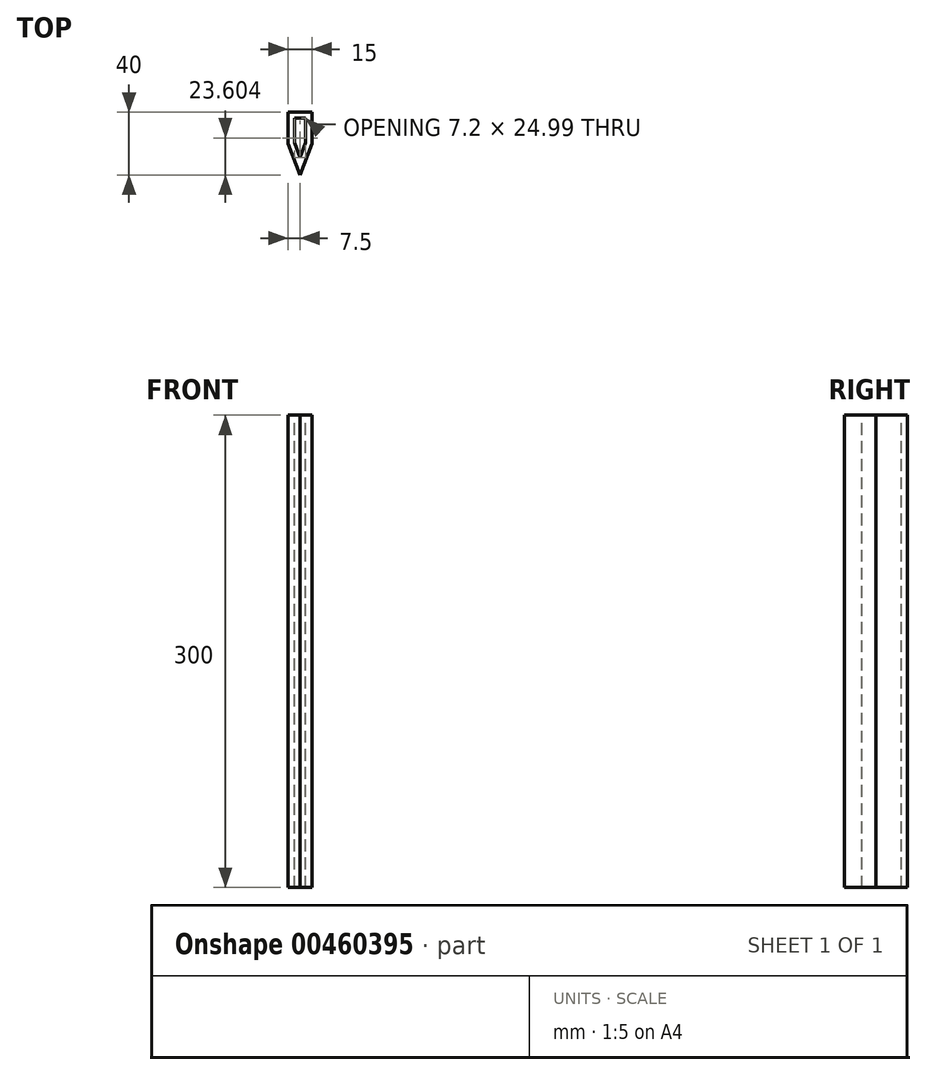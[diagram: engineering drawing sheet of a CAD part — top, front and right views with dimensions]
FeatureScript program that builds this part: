
annotation { "Feature Type Name" : "Feature", "Feature Type Description" : "" }
export const myFeature = defineFeature(function(context is Context, id is Id, definition is map)
    precondition{}
    {
        {
            var Q0;
            Q0=qCreatedBy(makeId("Top.planeOp"),FACE);
            var sketch = newSketch(context, id + "F0", { "sketchPlane" : qUnion([Q0])});
            skLineSegment(sketch, "E0", {"start": v(-7.5, 0) * mm, "end": v(-7.5, 20) * mm});
            skLineSegment(sketch, "E1", {"start": v(-7.5, 20) * mm, "end": v(7.5, 20) * mm});
            skLineSegment(sketch, "E2", {"start": v(7.5, 20) * mm, "end": v(7.5, 0) * mm});
            skLineSegment(sketch, "E3", {"start": v(7.5, 0) * mm, "end": v(0, -20) * mm});
            skLineSegment(sketch, "E4", {"start": v(0, -20) * mm, "end": v(-7.5, 0) * mm});
            skLineSegment(sketch, "E5", {"start": v(0, -20) * mm, "end": v(0, 20) * mm, "construction": true});
            skSolve(sketch);
        }
        {
            var Q0;
            Q0=makeQuery(id+"F0.imprint","IMPRINT",FACE,{"disambiguationData":[TD([[makeQuery(id+"F0.imprint","IMPRINT",EDGE,{"derivedFrom":sQuery(id+"F0.wireOp",EDGE,"E0")}),-1.0]])]});
            extrude(context, id + "F1", {"entities" : qUnion([Q0]), "depth" : 300 * mm, "offsetDistance" : 25 * mm});
        }
        {
            var Q0;
            Q0=makeQuery(id+"F1.opExtrude","CAP_FACE",FACE,{"disambiguationData":[OSD([sQuery(id+"F0.wireOp",EDGE,"E0"),sQuery(id+"F0.wireOp",EDGE,"E1"),sQuery(id+"F0.wireOp",EDGE,"E2"),sQuery(id+"F0.wireOp",EDGE,"E3"),sQuery(id+"F0.wireOp",EDGE,"E4")])],"isStart":false});
            var sketch = newSketch(context, id + "F2", { "sketchPlane" : qUnion([Q0])});
            skLineSegment(sketch, "E6.0", {"start": v(0, -8.9) * mm, "end": v(3.6, 0.7) * mm});
            skLineSegment(sketch, "E6.1", {"start": v(-3.6, 0.7) * mm, "end": v(0, -8.9) * mm});
            skLineSegment(sketch, "E6.2", {"start": v(3.6, 0.7) * mm, "end": v(3.6, 16.1) * mm});
            skLineSegment(sketch, "E6.3", {"start": v(3.6, 16.1) * mm, "end": v(-3.6, 16.1) * mm});
            skLineSegment(sketch, "E6.4", {"start": v(-3.6, 16.1) * mm, "end": v(-3.6, 0.7) * mm});
            skSolve(sketch);
        }
        {
            var Q0;
            Q0 = qSketchRegion(id + "F2", true);
            extrude(context, id + "F3", {"entities" : qUnion([Q0]), "operationType" : NewBodyOperationType.REMOVE, "endBound" : BoundingType.THROUGH_ALL, "oppositeDirection" : true, "depth" : 80 * mm, "offsetDistance" : 25 * mm});
        }
    });
